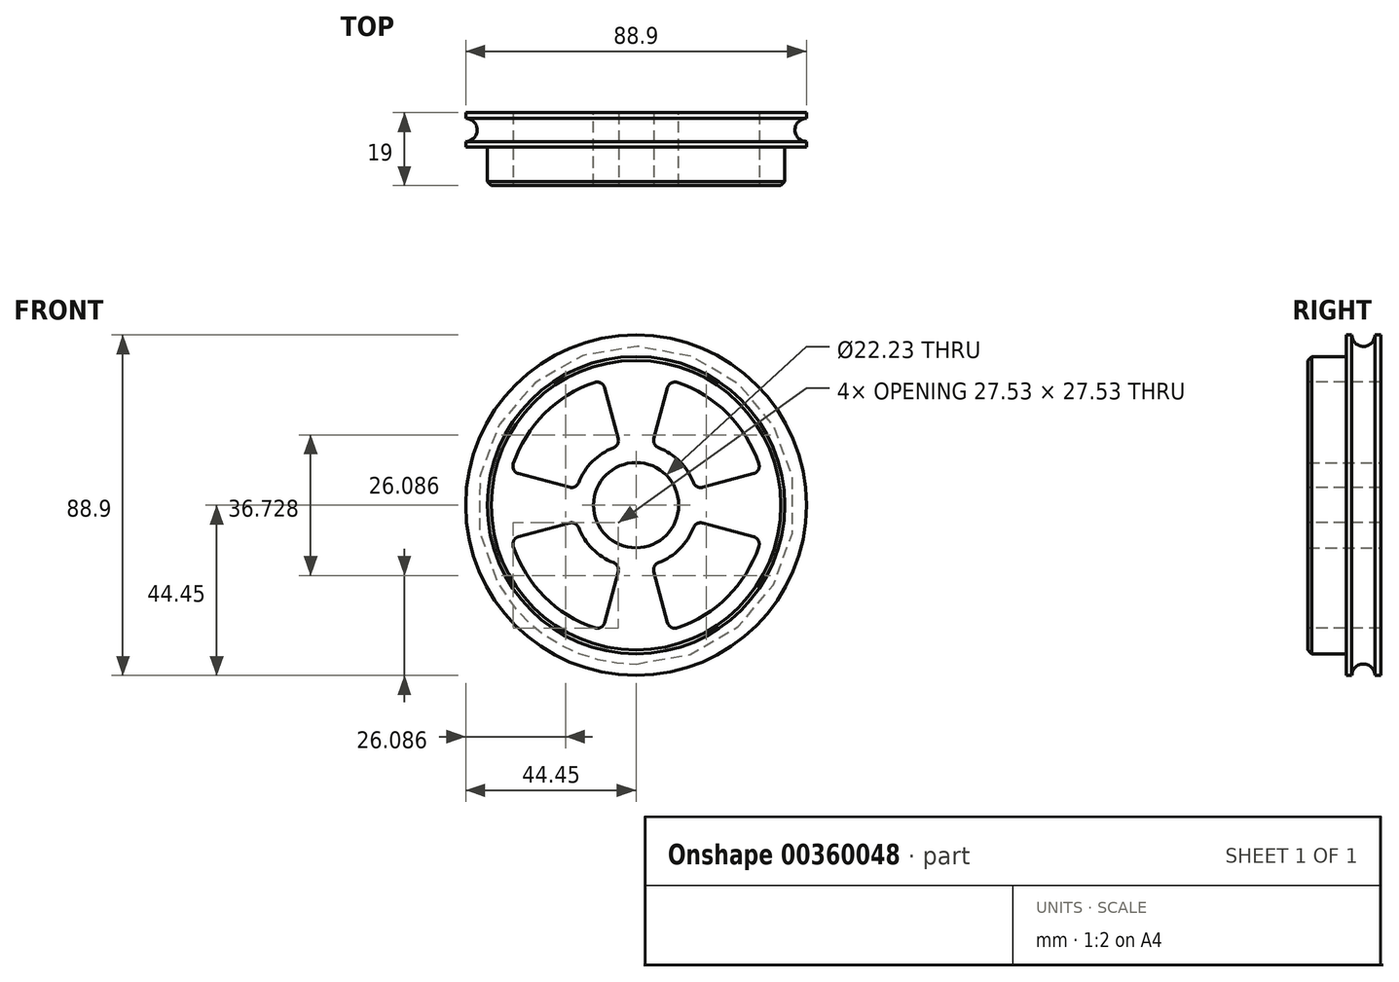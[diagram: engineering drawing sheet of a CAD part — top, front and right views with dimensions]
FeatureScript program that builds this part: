
annotation { "Feature Type Name" : "Feature", "Feature Type Description" : "" }
export const myFeature = defineFeature(function(context is Context, id is Id, definition is map)
    precondition{}
    {
        {
            var Q0;
            Q0=qCreatedBy(makeId("Front.planeOp"),FACE);
            var sketch = newSketch(context, id + "F0", { "sketchPlane" : qUnion([Q0])});
            skCircle(sketch, "E0", {"center": v(0, 0) * mm, "radius": 38.8 * mm});
            skCircle(sketch, "E1", {"center": v(0, 0) * mm, "radius": 11.11 * mm});
            skSolve(sketch);
        }
        {
            var Q0;
            Q0=makeQuery(id+"F0.imprint","IMPRINT",FACE,{"disambiguationData":[TD([[makeQuery(id+"F0.imprint","IMPRINT",EDGE,{"derivedFrom":sQuery(id+"F0.wireOp",EDGE,"E0")}),1.0]])]});
            extrude(context, id + "F1", {"entities" : qUnion([Q0]), "depth" : 12 * mm});
        }
        {
            var Q0;
            Q0=makeQuery(id+"F1.opExtrude","CAP_FACE",FACE,{"disambiguationData":[OSD([sQuery(id+"F0.wireOp",EDGE,"E0"),sQuery(id+"F0.wireOp",EDGE,"E1")])],"isStart":false});
            var sketch = newSketch(context, id + "F2", { "sketchPlane" : qUnion([Q0])});
            skCircle(sketch, "E2", {"center": v(0, 0) * mm, "radius": 44.45 * mm});
            skCircle(sketch, "E3", {"center": v(0, 0) * mm, "radius": 38.8 * mm});
            skLineSegment(sketch, "E4", {"start": v(0, 0) * mm, "end": v(0, -44.45) * mm, "construction": true});
            skLineSegment(sketch, "E5", {"start": v(0, 0) * mm, "end": v(5.8, -44.07) * mm});
            skLineSegment(sketch, "E6.MirrorCS", {"start": v(0, 0) * mm, "end": v(-5.8, -44.07) * mm});
            skLineSegment(sketch, "E7.1.0", {"start": v(0, 0) * mm, "end": v(35.26, 27.06) * mm});
            skLineSegment(sketch, "E7.1.1", {"start": v(0, 0) * mm, "end": v(41.07, 17.01) * mm});
            skLineSegment(sketch, "E7.2.0", {"start": v(0, 0) * mm, "end": v(-41.07, 17.01) * mm});
            skLineSegment(sketch, "E7.2.1", {"start": v(0, 0) * mm, "end": v(-35.26, 27.06) * mm});
            skSolve(sketch);
        }
        {
            var Q0;
            {var subQ0=sQuery(id+"F2.wireOp",EDGE,"E3");var subQ1=sQuery(id+"F2.wireOp",EDGE,"E2");Q0=makeQuery(id+"Fyo0gWlJh87S1LB_1.boolean.opBoolean","MERGE",FACE,{"derivedFrom":[makeQuery(id+"F1.opExtrude","CAP_FACE",FACE,{"disambiguationData":[OSD([sQuery(id+"F0.wireOp",EDGE,"E0"),sQuery(id+"F0.wireOp",EDGE,"E1")])],"isStart":false}),makeQuery(id+"Fyo0gWlJh87S1LB_1.opExtrude","CAP_FACE",FACE,{"disambiguationData":[OSD([subQ1,subQ0,sQuery(id+"F2.wireOp",EDGE,"E7.1.0"),sQuery(id+"F2.wireOp",EDGE,"E7.1.1")])],"isStart":true}),makeQuery(id+"Fyo0gWlJh87S1LB_1.opExtrude","CAP_FACE",FACE,{"disambiguationData":[OSD([subQ1,subQ0,sQuery(id+"F2.wireOp",EDGE,"E7.2.0"),sQuery(id+"F2.wireOp",EDGE,"E7.2.1")])],"isStart":true}),makeQuery(id+"Fyo0gWlJh87S1LB_1.opExtrude","CAP_FACE",FACE,{"disambiguationData":[OSD([subQ1,subQ0,sQuery(id+"F2.wireOp",EDGE,"E5"),sQuery(id+"F2.wireOp",EDGE,"E6.MirrorCS")])],"isStart":true})]});}
            var sketch = newSketch(context, id + "F3", { "sketchPlane" : qUnion([Q0])});
            skCircle(sketch, "E8", {"center": v(0, 0) * mm, "radius": 9.61 * mm});
            skCircle(sketch, "E9", {"center": v(0, 0) * mm, "radius": 11.11 * mm});
            skSolve(sketch);
        }
        {
            var Q0;
            {var subQ0=sQuery(id+"F2.wireOp",EDGE,"E3");var subQ1=sQuery(id+"F2.wireOp",EDGE,"E2");Q0=makeQuery(id+"Fyo0gWlJh87S1LB_1.boolean.opBoolean","MERGE",FACE,{"derivedFrom":[makeQuery(id+"F1.opExtrude","CAP_FACE",FACE,{"disambiguationData":[OSD([sQuery(id+"F0.wireOp",EDGE,"E0"),sQuery(id+"F0.wireOp",EDGE,"E1")])],"isStart":false}),makeQuery(id+"Fyo0gWlJh87S1LB_1.opExtrude","CAP_FACE",FACE,{"disambiguationData":[OSD([subQ1,subQ0,sQuery(id+"F2.wireOp",EDGE,"27980060-e5c7-4240-b4d6-3186c7cb0f6e.2.0"),sQuery(id+"F2.wireOp",EDGE,"27980060-e5c7-4240-b4d6-3186c7cb0f6e.2.1")])],"isStart":true}),makeQuery(id+"Fyo0gWlJh87S1LB_1.opExtrude","CAP_FACE",FACE,{"disambiguationData":[OSD([subQ1,subQ0,sQuery(id+"F2.wireOp",EDGE,"27980060-e5c7-4240-b4d6-3186c7cb0f6e.1.0"),sQuery(id+"F2.wireOp",EDGE,"27980060-e5c7-4240-b4d6-3186c7cb0f6e.1.1")])],"isStart":true}),makeQuery(id+"Fyo0gWlJh87S1LB_1.opExtrude","CAP_FACE",FACE,{"disambiguationData":[OSD([subQ1,subQ0,sQuery(id+"F2.wireOp",EDGE,"E5"),sQuery(id+"F2.wireOp",EDGE,"E6.MirrorCS")])],"isStart":true}),makeQuery(id+"Fyo0gWlJh87S1LB_1.opExtrude","CAP_FACE",FACE,{"disambiguationData":[OSD([subQ1,subQ0,sQuery(id+"F2.wireOp",EDGE,"27980060-e5c7-4240-b4d6-3186c7cb0f6e.3.0"),sQuery(id+"F2.wireOp",EDGE,"27980060-e5c7-4240-b4d6-3186c7cb0f6e.3.1")])],"isStart":true})]});}
            var sketch = newSketch(context, id + "F4", { "sketchPlane" : qUnion([Q0])});
            skLineSegment(sketch, "E10", {"start": v(0, 0) * mm, "end": v(0, -44.45) * mm, "construction": true});
            skCircle(sketch, "E11", {"center": v(0, 0) * mm, "radius": 33.8 * mm});
            skLineSegment(sketch, "E12", {"start": v(0, 0) * mm, "end": v(8.75, -32.65) * mm});
            skLineSegment(sketch, "E13.MirrorCS", {"start": v(0, 0) * mm, "end": v(-8.75, -32.65) * mm});
            skLineSegment(sketch, "E14.1.0", {"start": v(0, 0) * mm, "end": v(32.65, 8.75) * mm});
            skLineSegment(sketch, "E14.1.1", {"start": v(0, 0) * mm, "end": v(32.65, -8.75) * mm});
            skLineSegment(sketch, "E14.2.0", {"start": v(0, 0) * mm, "end": v(-8.75, 32.65) * mm});
            skLineSegment(sketch, "E14.2.1", {"start": v(0, 0) * mm, "end": v(8.75, 32.65) * mm});
            skLineSegment(sketch, "E14.3.0", {"start": v(0, 0) * mm, "end": v(-32.65, -8.75) * mm});
            skLineSegment(sketch, "E14.3.1", {"start": v(0, 0) * mm, "end": v(-32.65, 8.75) * mm});
            skCircle(sketch, "E15", {"center": v(0, 0) * mm, "radius": 16.11 * mm});
            skSolve(sketch);
        }
        {
            var Q0;
            {var subQ0=sQuery(id+"F4.wireOp",EDGE,"E12");var subQ1=sQuery(id+"F4.wireOp",EDGE,"E11");var subQ2=makeQuery(id+"F4.imprint","INTERSECT",VERTEX,{"derivedFrom":[subQ1,subQ0]});Q0=makeQuery(id+"F4.imprint","IMPRINT",FACE,{"disambiguationData":[TD([[makeQuery(id+"F4.imprint","IMPRINT",EDGE,{"disambiguationData":[TD([[subQ2,-1.0]])],"derivedFrom":subQ1}),1.0]])]});}
            var Q1;
            {var subQ0=sQuery(id+"F4.wireOp",EDGE,"E13.MirrorCS");var subQ1=sQuery(id+"F4.wireOp",EDGE,"E11");var subQ2=makeQuery(id+"F4.imprint","INTERSECT",VERTEX,{"derivedFrom":[subQ1,subQ0]});Q1=makeQuery(id+"F4.imprint","IMPRINT",FACE,{"disambiguationData":[TD([[makeQuery(id+"F4.imprint","IMPRINT",EDGE,{"disambiguationData":[TD([[subQ2,1.0]])],"derivedFrom":subQ1}),1.0]])]});}
            var Q2;
            {var subQ0=sQuery(id+"F4.wireOp",EDGE,"E14.2.0");var subQ1=sQuery(id+"F4.wireOp",EDGE,"E11");var subQ2=makeQuery(id+"F4.imprint","INTERSECT",VERTEX,{"derivedFrom":[subQ1,subQ0]});Q2=makeQuery(id+"F4.imprint","IMPRINT",FACE,{"disambiguationData":[TD([[makeQuery(id+"F4.imprint","IMPRINT",EDGE,{"disambiguationData":[TD([[subQ2,-1.0]])],"derivedFrom":subQ1}),1.0]])]});}
            var Q3;
            {var subQ0=sQuery(id+"F4.wireOp",EDGE,"E14.1.0");var subQ1=sQuery(id+"F4.wireOp",EDGE,"E11");var subQ2=makeQuery(id+"F4.imprint","INTERSECT",VERTEX,{"derivedFrom":[subQ1,subQ0]});Q3=makeQuery(id+"F4.imprint","IMPRINT",FACE,{"disambiguationData":[TD([[makeQuery(id+"F4.imprint","IMPRINT",EDGE,{"disambiguationData":[TD([[subQ2,-1.0]])],"derivedFrom":subQ1}),1.0]])]});}
            extrude(context, id + "F5", {"entities" : qUnion([Q0, Q1, Q2, Q3]), "operationType" : NewBodyOperationType.REMOVE, "oppositeDirection" : true, "depth" : 25 * mm});
        }
        {
            var Q0;
            Q0=makeQuery(id+"F5.boolean.opBoolean","COPY",EDGE,{"derivedFrom":makeQuery(id+"F5.opExtrude","SWEPT_EDGE",EDGE,{"disambiguationData":[OSD([sQuery(id+"F4.wireOp",EDGE,"E11"),sQuery(id+"F4.wireOp",EDGE,"E13.MirrorCS")])]})});
            var Q1;
            Q1=makeQuery(id+"F5.boolean.opBoolean","COPY",EDGE,{"derivedFrom":makeQuery(id+"F5.opExtrude","SWEPT_EDGE",EDGE,{"disambiguationData":[OSD([sQuery(id+"F4.wireOp",EDGE,"E13.MirrorCS"),sQuery(id+"F4.wireOp",EDGE,"E15")])]})});
            var Q2;
            Q2=makeQuery(id+"F5.boolean.opBoolean","COPY",EDGE,{"derivedFrom":makeQuery(id+"F5.opExtrude","SWEPT_EDGE",EDGE,{"disambiguationData":[OSD([sQuery(id+"F4.wireOp",EDGE,"E14.3.0"),sQuery(id+"F4.wireOp",EDGE,"E15")])]})});
            var Q3;
            Q3=makeQuery(id+"F5.boolean.opBoolean","COPY",EDGE,{"derivedFrom":makeQuery(id+"F5.opExtrude","SWEPT_EDGE",EDGE,{"disambiguationData":[OSD([sQuery(id+"F4.wireOp",EDGE,"E11"),sQuery(id+"F4.wireOp",EDGE,"E14.3.0")])]})});
            var Q4;
            Q4=makeQuery(id+"F5.boolean.opBoolean","COPY",EDGE,{"derivedFrom":makeQuery(id+"F5.opExtrude","SWEPT_EDGE",EDGE,{"disambiguationData":[OSD([sQuery(id+"F4.wireOp",EDGE,"E12"),sQuery(id+"F4.wireOp",EDGE,"E15")])]})});
            var Q5;
            Q5=makeQuery(id+"F5.boolean.opBoolean","COPY",EDGE,{"derivedFrom":makeQuery(id+"F5.opExtrude","SWEPT_EDGE",EDGE,{"disambiguationData":[OSD([sQuery(id+"F4.wireOp",EDGE,"E11"),sQuery(id+"F4.wireOp",EDGE,"E12")])]})});
            var Q6;
            Q6=makeQuery(id+"F5.boolean.opBoolean","COPY",EDGE,{"derivedFrom":makeQuery(id+"F5.opExtrude","SWEPT_EDGE",EDGE,{"disambiguationData":[OSD([sQuery(id+"F4.wireOp",EDGE,"E14.1.1"),sQuery(id+"F4.wireOp",EDGE,"E15")])]})});
            var Q7;
            Q7=makeQuery(id+"F5.boolean.opBoolean","COPY",EDGE,{"derivedFrom":makeQuery(id+"F5.opExtrude","SWEPT_EDGE",EDGE,{"disambiguationData":[OSD([sQuery(id+"F4.wireOp",EDGE,"E11"),sQuery(id+"F4.wireOp",EDGE,"E14.1.1")])]})});
            var Q8;
            Q8=makeQuery(id+"F5.boolean.opBoolean","COPY",EDGE,{"derivedFrom":makeQuery(id+"F5.opExtrude","SWEPT_EDGE",EDGE,{"disambiguationData":[OSD([sQuery(id+"F4.wireOp",EDGE,"E11"),sQuery(id+"F4.wireOp",EDGE,"E14.2.1")])]})});
            var Q9;
            Q9=makeQuery(id+"F5.boolean.opBoolean","COPY",EDGE,{"derivedFrom":makeQuery(id+"F5.opExtrude","SWEPT_EDGE",EDGE,{"disambiguationData":[OSD([sQuery(id+"F4.wireOp",EDGE,"E11"),sQuery(id+"F4.wireOp",EDGE,"E14.1.0")])]})});
            var Q10;
            Q10=makeQuery(id+"F5.boolean.opBoolean","COPY",EDGE,{"derivedFrom":makeQuery(id+"F5.opExtrude","SWEPT_EDGE",EDGE,{"disambiguationData":[OSD([sQuery(id+"F4.wireOp",EDGE,"E14.1.0"),sQuery(id+"F4.wireOp",EDGE,"E15")])]})});
            var Q11;
            Q11=makeQuery(id+"F5.boolean.opBoolean","COPY",EDGE,{"derivedFrom":makeQuery(id+"F5.opExtrude","SWEPT_EDGE",EDGE,{"disambiguationData":[OSD([sQuery(id+"F4.wireOp",EDGE,"E14.2.1"),sQuery(id+"F4.wireOp",EDGE,"E15")])]})});
            var Q12;
            Q12=makeQuery(id+"F5.boolean.opBoolean","COPY",EDGE,{"derivedFrom":makeQuery(id+"F5.opExtrude","SWEPT_EDGE",EDGE,{"disambiguationData":[OSD([sQuery(id+"F4.wireOp",EDGE,"E14.2.0"),sQuery(id+"F4.wireOp",EDGE,"E15")])]})});
            var Q13;
            Q13=makeQuery(id+"F5.boolean.opBoolean","COPY",EDGE,{"derivedFrom":makeQuery(id+"F5.opExtrude","SWEPT_EDGE",EDGE,{"disambiguationData":[OSD([sQuery(id+"F4.wireOp",EDGE,"E14.3.1"),sQuery(id+"F4.wireOp",EDGE,"E15")])]})});
            var Q14;
            Q14=makeQuery(id+"F5.boolean.opBoolean","COPY",EDGE,{"derivedFrom":makeQuery(id+"F5.opExtrude","SWEPT_EDGE",EDGE,{"disambiguationData":[OSD([sQuery(id+"F4.wireOp",EDGE,"E11"),sQuery(id+"F4.wireOp",EDGE,"E14.2.0")])]})});
            var Q15;
            Q15=makeQuery(id+"F5.boolean.opBoolean","COPY",EDGE,{"derivedFrom":makeQuery(id+"F5.opExtrude","SWEPT_EDGE",EDGE,{"disambiguationData":[OSD([sQuery(id+"F4.wireOp",EDGE,"E11"),sQuery(id+"F4.wireOp",EDGE,"E14.3.1")])]})});
            var Q16;
            Q16=makeQuery(id+"Fyo0gWlJh87S1LB_1.opExtrude","SWEPT_EDGE",EDGE,{"disambiguationData":[OSD([sQuery(id+"F2.wireOp",EDGE,"E3"),sQuery(id+"F2.wireOp",EDGE,"27980060-e5c7-4240-b4d6-3186c7cb0f6e.3.1")])]});
            var Q17;
            Q17=makeQuery(id+"Fyo0gWlJh87S1LB_1.opExtrude","SWEPT_EDGE",EDGE,{"disambiguationData":[OSD([sQuery(id+"F2.wireOp",EDGE,"E3"),sQuery(id+"F2.wireOp",EDGE,"E5")])]});
            var Q18;
            Q18=makeQuery(id+"Fyo0gWlJh87S1LB_1.opExtrude","SWEPT_EDGE",EDGE,{"disambiguationData":[OSD([sQuery(id+"F2.wireOp",EDGE,"E3"),sQuery(id+"F2.wireOp",EDGE,"E6.MirrorCS")])]});
            var Q19;
            Q19=makeQuery(id+"Fyo0gWlJh87S1LB_1.opExtrude","SWEPT_EDGE",EDGE,{"disambiguationData":[OSD([sQuery(id+"F2.wireOp",EDGE,"E3"),sQuery(id+"F2.wireOp",EDGE,"27980060-e5c7-4240-b4d6-3186c7cb0f6e.1.0")])]});
            var Q20;
            Q20=makeQuery(id+"Fyo0gWlJh87S1LB_1.opExtrude","SWEPT_EDGE",EDGE,{"disambiguationData":[OSD([sQuery(id+"F2.wireOp",EDGE,"E3"),sQuery(id+"F2.wireOp",EDGE,"27980060-e5c7-4240-b4d6-3186c7cb0f6e.1.1")])]});
            var Q21;
            Q21=makeQuery(id+"Fyo0gWlJh87S1LB_1.opExtrude","SWEPT_EDGE",EDGE,{"disambiguationData":[OSD([sQuery(id+"F2.wireOp",EDGE,"E3"),sQuery(id+"F2.wireOp",EDGE,"27980060-e5c7-4240-b4d6-3186c7cb0f6e.2.0")])]});
            var Q22;
            Q22=makeQuery(id+"Fyo0gWlJh87S1LB_1.opExtrude","SWEPT_EDGE",EDGE,{"disambiguationData":[OSD([sQuery(id+"F2.wireOp",EDGE,"E3"),sQuery(id+"F2.wireOp",EDGE,"27980060-e5c7-4240-b4d6-3186c7cb0f6e.2.1")])]});
            var Q23;
            Q23=makeQuery(id+"Fyo0gWlJh87S1LB_1.opExtrude","SWEPT_EDGE",EDGE,{"disambiguationData":[OSD([sQuery(id+"F2.wireOp",EDGE,"E3"),sQuery(id+"F2.wireOp",EDGE,"27980060-e5c7-4240-b4d6-3186c7cb0f6e.3.0")])]});
            fillet(context, id + "F6", {"entities" : qUnion([Q0, Q1, Q2, Q3, Q4, Q5, Q6, Q7, Q8, Q9, Q10, Q11, Q12, Q13, Q14, Q15, Q16, Q17, Q18, Q19, Q20, Q21, Q22, Q23]), "radius" : 2 * mm, "tangentPropagation" : true, "allowEdgeOverflow" : false});
        }
        {
            var Q0;
            Q0=makeQuery(id+"F1.opExtrude","CAP_FACE",FACE,{"disambiguationData":[OSD([sQuery(id+"F0.wireOp",EDGE,"E0"),sQuery(id+"F0.wireOp",EDGE,"E1")])],"isStart":true});
            var sketch = newSketch(context, id + "F7", { "sketchPlane" : qUnion([Q0])});
            skCircle(sketch, "E16", {"center": v(0, 0) * mm, "radius": 38.8 * mm});
            skCircle(sketch, "E17", {"center": v(0, 0) * mm, "radius": 33.8 * mm});
            skSolve(sketch);
        }
        {
            var Q0;
            Q0=qCreatedBy(makeId("Right.planeOp"),FACE);
            var sketch = newSketch(context, id + "F8", { "sketchPlane" : qUnion([Q0])});
            skLineSegment(sketch, "E18", {"start": v(-12, 38.8) * mm, "end": v(0, 38.8) * mm, "construction": true});
            skLineSegment(sketch, "E19.0", {"start": v(0, 33.8) * mm, "end": v(0, -33.8) * mm, "construction": true});
            skLineSegment(sketch, "E20", {"start": v(0.67, 0) * mm, "end": v(8, 0) * mm, "construction": true});
            skArc(sketch, "E21", {"start": v(-0.5, 44.45) * mm, "mid": v(2.5, 41.45) * mm, "end": v(5.5, 44.45) * mm});
            skLineSegment(sketch, "E22", {"start": v(5.5, 44.45) * mm, "end": v(7, 44.45) * mm});
            skLineSegment(sketch, "E23", {"start": v(7, 44.45) * mm, "end": v(7, 33.8) * mm});
            skLineSegment(sketch, "E24", {"start": v(0, 33.8) * mm, "end": v(7, 33.8) * mm});
            skLineSegment(sketch, "E25", {"start": v(0, 38.8) * mm, "end": v(0, 33.8) * mm});
            skLineSegment(sketch, "E26", {"start": v(-2, 38.8) * mm, "end": v(-2, 44.45) * mm});
            skLineSegment(sketch, "E27", {"start": v(-2, 38.8) * mm, "end": v(0, 38.8) * mm});
            skLineSegment(sketch, "E28", {"start": v(-2, 44.45) * mm, "end": v(-0.5, 44.45) * mm});
            skSolve(sketch);
        }
        {
            var Q0;
            Q0=makeQuery(id+"F8.imprint","IMPRINT",FACE,{"disambiguationData":[TD([[makeQuery(id+"F8.imprint","IMPRINT",EDGE,{"derivedFrom":sQuery(id+"F8.wireOp",EDGE,"E21")}),-1.0]])]});
            var Q1;
            Q1=sQuery(id+"F8.wireOp",EDGE,"E20");
            revolve(context, id + "F9", {"operationType" : NewBodyOperationType.ADD, "entities" : qUnion([Q0]), "axis" : qUnion([Q1]), "revolveType" : RevolveType.FULL});
        }
        {
            var Q0;
            Q0=makeQuery(id+"F1.opExtrude","CAP_EDGE",EDGE,{"disambiguationData":[OSD([sQuery(id+"F0.wireOp",EDGE,"E0")])],"isStart":false});
            chamfer(context, id + "F10", {"entities" : qUnion([Q0]), "width" : 1 * mm, "tangentPropagation" : true});
        }
        {
            var Q0;
            Q0=makeQuery(id+"F1.opExtrude","CAP_FACE",FACE,{"disambiguationData":[OSD([sQuery(id+"F0.wireOp",EDGE,"E0"),sQuery(id+"F0.wireOp",EDGE,"E1")])],"isStart":true});
            var Q1;
            Q1=makeQuery(id+"F9.opRevolve","SWEPT_FACE",FACE,{"disambiguationData":[OSD([sQuery(id+"F8.wireOp",EDGE,"E23")])]});
            extrude(context, id + "F11", {"entities" : qUnion([Q0]), "operationType" : NewBodyOperationType.ADD, "endBound" : BoundingType.UP_TO_SURFACE, "endBoundEntityFace" : qUnion([Q1]), "depth" : 25 * mm});
        }
    });
